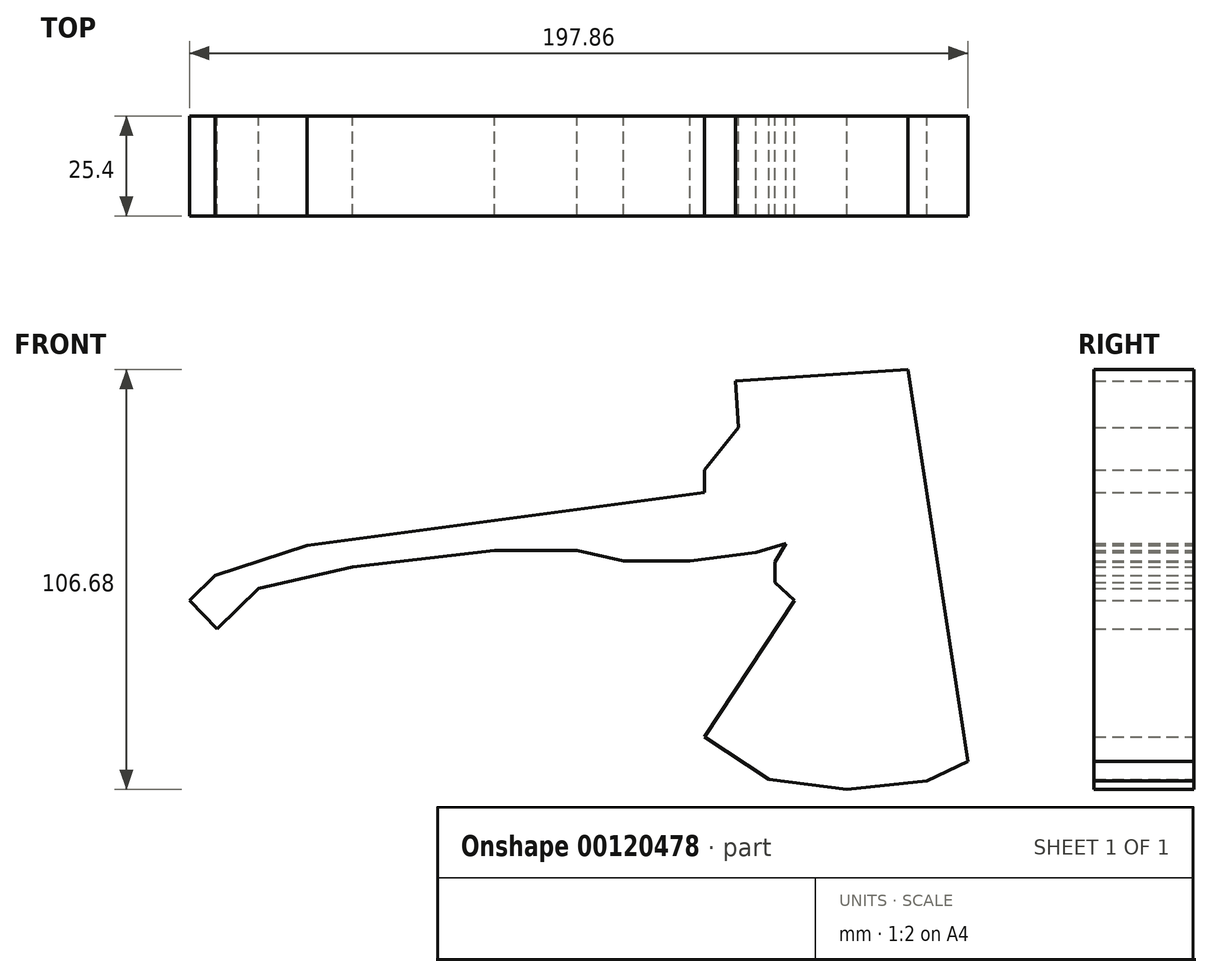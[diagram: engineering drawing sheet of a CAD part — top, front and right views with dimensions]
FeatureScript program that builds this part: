
annotation { "Feature Type Name" : "Feature", "Feature Type Description" : "" }
export const myFeature = defineFeature(function(context is Context, id is Id, definition is map)
    precondition{}
    {
        {
            var Q0;
            Q0=qCreatedBy(makeId("Front.planeOp"),FACE);
            var sketch = newSketch(context, id + "F0", { "sketchPlane" : qUnion([Q0])});
            skLineSegment(sketch, "E0", {"start": v(-92.75, 14.05) * mm, "end": v(-116.14, 6.43) * mm});
            skLineSegment(sketch, "E1", {"start": v(-116.14, 6.43) * mm, "end": v(-122.7, 0) * mm});
            skLineSegment(sketch, "E2", {"start": v(-122.7, 0) * mm, "end": v(-115.62, -7.23) * mm});
            skLineSegment(sketch, "E3", {"start": v(-115.62, -7.23) * mm, "end": v(-105.13, 3.04) * mm});
            skLineSegment(sketch, "E4", {"start": v(-105.13, 3.04) * mm, "end": v(-81.2, 8.54) * mm});
            skLineSegment(sketch, "E5", {"start": v(-81.2, 8.54) * mm, "end": v(-45.2, 12.74) * mm});
            skLineSegment(sketch, "E6", {"start": v(-45.2, 12.74) * mm, "end": v(-24.17, 12.74) * mm});
            skLineSegment(sketch, "E7", {"start": v(-24.17, 12.74) * mm, "end": v(-12.35, 10.11) * mm});
            skLineSegment(sketch, "E8", {"start": v(-12.35, 10.11) * mm, "end": v(4.47, 10.11) * mm});
            skLineSegment(sketch, "E9", {"start": v(4.47, 10.11) * mm, "end": v(21.28, 12.22) * mm});
            skLineSegment(sketch, "E10", {"start": v(21.28, 12.22) * mm, "end": v(28.9, 14.58) * mm});
            skLineSegment(sketch, "E11", {"start": v(28.9, 14.58) * mm, "end": v(26.01, 9.85) * mm});
            skLineSegment(sketch, "E12", {"start": v(26.01, 9.85) * mm, "end": v(26.01, 4.6) * mm});
            skLineSegment(sketch, "E13", {"start": v(26.01, 4.6) * mm, "end": v(31, 0) * mm});
            skLineSegment(sketch, "E14", {"start": v(31, 0) * mm, "end": v(8.15, -34.56) * mm});
            skLineSegment(sketch, "E15", {"start": v(8.15, -34.56) * mm, "end": v(24.56, -45.42) * mm});
            skLineSegment(sketch, "E16", {"start": v(24.56, -45.42) * mm, "end": v(44.4, -47.96) * mm});
            skLineSegment(sketch, "E17", {"start": v(44.4, -47.96) * mm, "end": v(64.64, -45.85) * mm});
            skLineSegment(sketch, "E18", {"start": v(64.64, -45.85) * mm, "end": v(75.15, -40.86) * mm});
            skLineSegment(sketch, "E19", {"start": v(75.15, -40.86) * mm, "end": v(59.9, 58.72) * mm});
            skLineSegment(sketch, "E20", {"start": v(59.9, 58.72) * mm, "end": v(16.03, 55.83) * mm});
            skLineSegment(sketch, "E21", {"start": v(16.03, 55.83) * mm, "end": v(16.8, 44) * mm});
            skLineSegment(sketch, "E22", {"start": v(16.8, 44) * mm, "end": v(8.15, 33.24) * mm});
            skLineSegment(sketch, "E23", {"start": v(8.15, 33.24) * mm, "end": v(8.15, 27.46) * mm});
            skLineSegment(sketch, "E24", {"start": v(8.15, 27.46) * mm, "end": v(-92.75, 14.05) * mm});
            skSolve(sketch);
        }
        {
            var Q0;
            Q0=makeQuery(id+"F0.imprint","IMPRINT",FACE,{"disambiguationData":[TD([[makeQuery(id+"F0.imprint","IMPRINT",EDGE,{"derivedFrom":sQuery(id+"F0.wireOp",EDGE,"E0")}),1.0]])]});
            var Q1;
            Q1=sQuery(id+"F0.wireOp",EDGE,"E15");
            var Q2;
            Q2=sQuery(id+"F0.wireOp",EDGE,"E14");
            var Q3;
            Q3=sQuery(id+"F0.wireOp",EDGE,"E19");
            var Q4;
            Q4=sQuery(id+"F0.wireOp",EDGE,"E21");
            var Q5;
            Q5=sQuery(id+"F0.wireOp",EDGE,"E17");
            var Q6;
            Q6=sQuery(id+"F0.wireOp",EDGE,"E24");
            var Q7;
            Q7=sQuery(id+"F0.wireOp",EDGE,"E0");
            var Q8;
            Q8=sQuery(id+"F0.wireOp",EDGE,"E1");
            var Q9;
            Q9=sQuery(id+"F0.wireOp",EDGE,"E10");
            var Q10;
            Q10=sQuery(id+"F0.wireOp",EDGE,"E22");
            var Q11;
            Q11=sQuery(id+"F0.wireOp",EDGE,"E20");
            var Q12;
            Q12=sQuery(id+"F0.wireOp",EDGE,"E9");
            var Q13;
            Q13=sQuery(id+"F0.wireOp",EDGE,"E3");
            var Q14;
            Q14=sQuery(id+"F0.wireOp",EDGE,"E2");
            var Q15;
            Q15=sQuery(id+"F0.wireOp",EDGE,"E8");
            var Q16;
            Q16=sQuery(id+"F0.wireOp",EDGE,"E7");
            var Q17;
            Q17=sQuery(id+"F0.wireOp",EDGE,"E18");
            var Q18;
            Q18=sQuery(id+"F0.wireOp",EDGE,"E6");
            var Q19;
            Q19=sQuery(id+"F0.wireOp",EDGE,"E4");
            var Q20;
            Q20=sQuery(id+"F0.wireOp",EDGE,"E5");
            var Q21;
            Q21=sQuery(id+"F0.wireOp",EDGE,"E16");
            var Q22;
            Q22=sQuery(id+"F0.wireOp",EDGE,"E12");
            var Q23;
            Q23=sQuery(id+"F0.wireOp",EDGE,"E13");
            var Q24;
            Q24=sQuery(id+"F0.wireOp",EDGE,"E23");
            var Q25;
            Q25=sQuery(id+"F0.wireOp",EDGE,"E11");
            extrude(context, id + "F1", {"entities" : qUnion([Q0]), "surfaceEntities" : qUnion([Q1, Q2, Q3, Q4, Q5, Q6, Q7, Q8, Q9, Q10, Q11, Q12, Q13, Q14, Q15, Q16, Q17, Q18, Q19, Q20, Q21, Q22, Q23, Q24, Q25]), "endBound" : BoundingType.SYMMETRIC, "depth" : 25.4 * mm});
        }
    });
